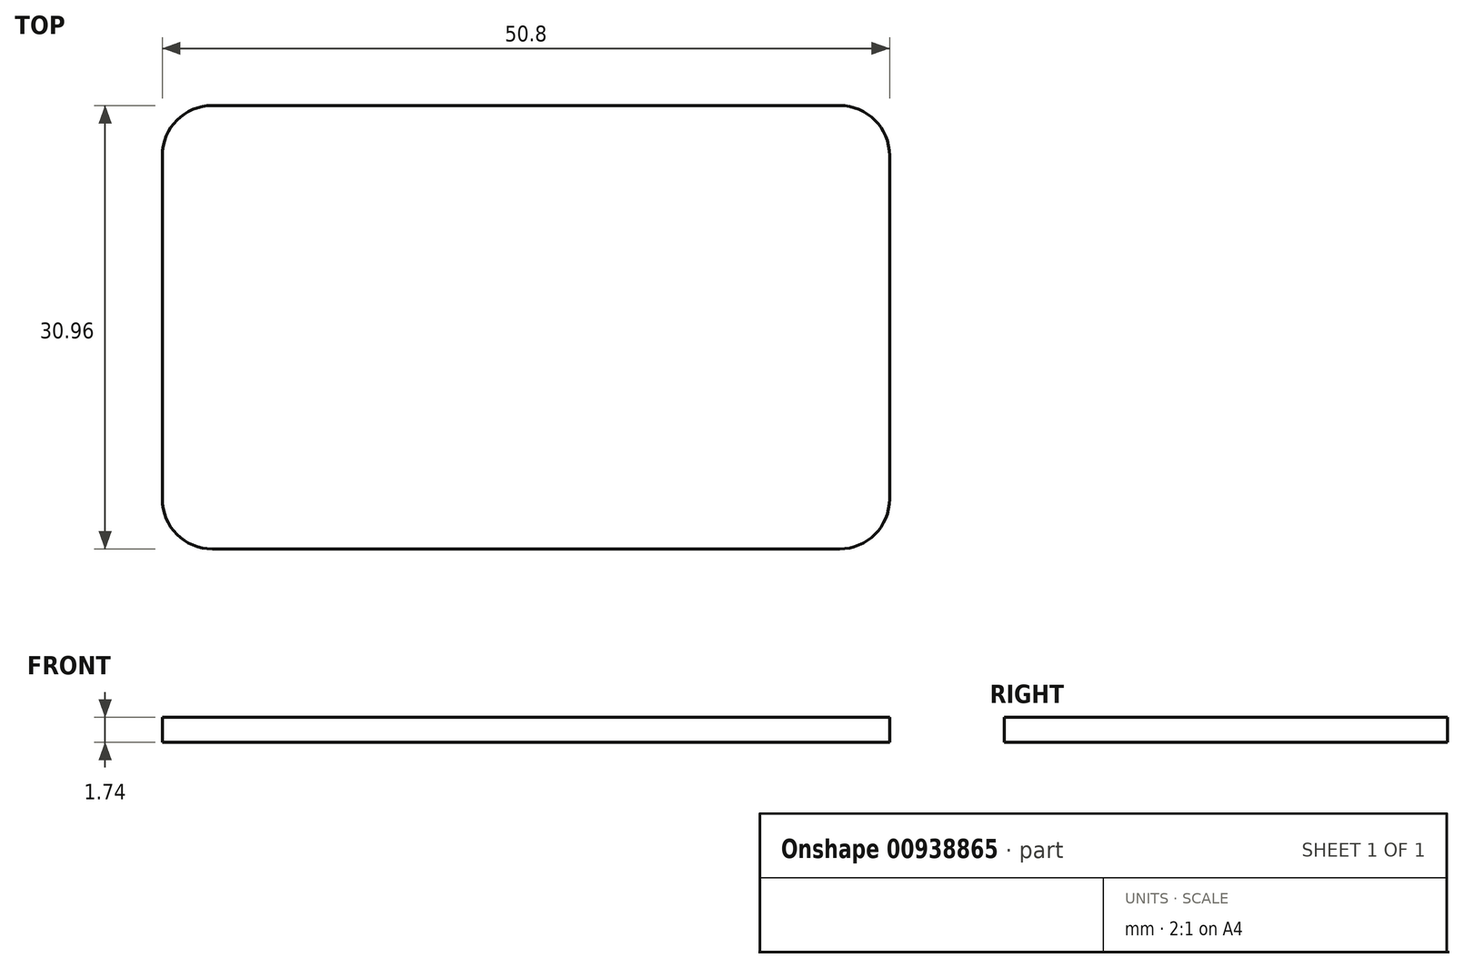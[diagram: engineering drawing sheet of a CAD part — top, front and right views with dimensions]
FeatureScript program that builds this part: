
annotation { "Feature Type Name" : "Feature", "Feature Type Description" : "" }
export const myFeature = defineFeature(function(context is Context, id is Id, definition is map)
    precondition{}
    {
        {
            var Q0;
            Q0=qCreatedBy(makeId("Top.planeOp"),FACE);
            var sketch = newSketch(context, id + "F0", { "sketchPlane" : qUnion([Q0])});
            skLineSegment(sketch, "E0.bottom", {"start": v(0, 0) * mm, "end": v(50.8, 0) * mm});
            skLineSegment(sketch, "E0.top", {"start": v(0, 30.96) * mm, "end": v(50.8, 30.96) * mm});
            skLineSegment(sketch, "E0.left", {"start": v(0, 0) * mm, "end": v(0, 30.96) * mm});
            skLineSegment(sketch, "E0.right", {"start": v(50.8, 0) * mm, "end": v(50.8, 30.96) * mm});
            skSolve(sketch);
        }
        {
            var Q0;
            Q0 = qSketchRegion(id + "F0", true);
            extrude(context, id + "F1", {"entities" : qUnion([Q0]), "depth" : 1.74 * mm, "offsetDistance" : 25.4 * mm});
        }
        {
            var Q0;
            Q0=makeQuery(id+"F1.opExtrude","SWEPT_EDGE",EDGE,{"disambiguationData":[OSD([sQuery(id+"F0.wireOp",EDGE,"E0.bottom"),sQuery(id+"F0.wireOp",EDGE,"E0.right")])]});
            var Q1;
            Q1=makeQuery(id+"F1.opExtrude","SWEPT_EDGE",EDGE,{"disambiguationData":[OSD([sQuery(id+"F0.wireOp",EDGE,"E0.top"),sQuery(id+"F0.wireOp",EDGE,"E0.right")])]});
            var Q2;
            Q2=makeQuery(id+"F1.opExtrude","SWEPT_EDGE",EDGE,{"disambiguationData":[OSD([sQuery(id+"F0.wireOp",EDGE,"E0.top"),sQuery(id+"F0.wireOp",EDGE,"E0.left")])]});
            var Q3;
            Q3=makeQuery(id+"F1.opExtrude","SWEPT_EDGE",EDGE,{"disambiguationData":[OSD([sQuery(id+"F0.wireOp",EDGE,"E0.bottom"),sQuery(id+"F0.wireOp",EDGE,"E0.left")])]});
            fillet(context, id + "F2", {"entities" : qUnion([Q0, Q1, Q2, Q3]), "radius" : 3.5 * mm, "tangentPropagation" : true, "allowEdgeOverflow" : false});
        }
    });
